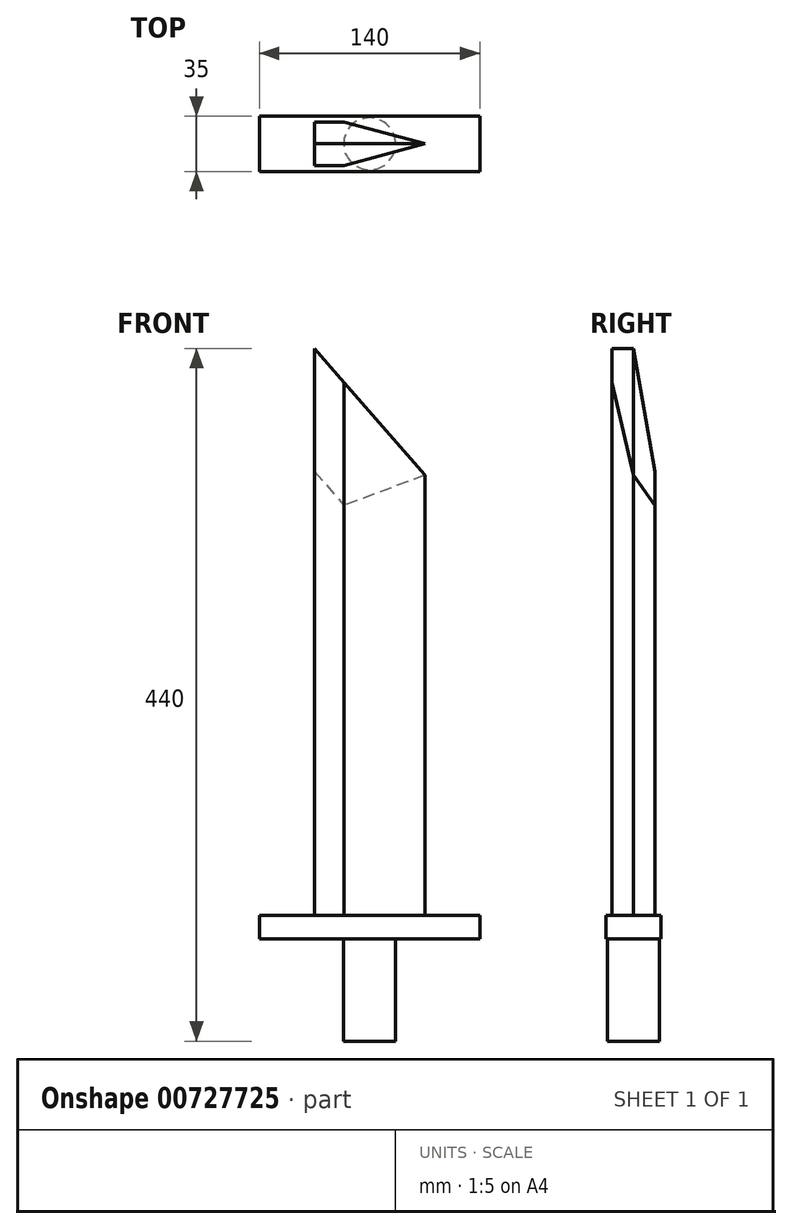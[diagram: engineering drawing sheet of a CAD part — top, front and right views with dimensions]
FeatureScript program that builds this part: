
annotation { "Feature Type Name" : "Feature", "Feature Type Description" : "" }
export const myFeature = defineFeature(function(context is Context, id is Id, definition is map)
    precondition{}
    {
        {
            var Q0;
            Q0=qCreatedBy(makeId("Top.planeOp"),FACE);
            var sketch = newSketch(context, id + "F0", { "sketchPlane" : qUnion([Q0])});
            skCircle(sketch, "E0", {"center": v(0, 0) * mm, "radius": 16.5 * mm});
            skSolve(sketch);
        }
        {
            var Q0;
            Q0=makeQuery(id+"F0.imprint","IMPRINT",FACE,{"disambiguationData":[TD([[makeQuery(id+"F0.imprint","IMPRINT",EDGE,{"derivedFrom":sQuery(id+"F0.wireOp",EDGE,"E0")}),1.0]])]});
            extrude(context, id + "F1", {"entities" : qUnion([Q0]), "oppositeDirection" : true, "depth" : 80 * mm, "offsetDistance" : 25 * mm});
        }
        {
            var Q0;
            Q0=makeQuery(id+"F1.opExtrude","CAP_FACE",FACE,{"disambiguationData":[OSD([sQuery(id+"F0.wireOp",EDGE,"E0")])],"isStart":true});
            var sketch = newSketch(context, id + "F2", { "sketchPlane" : qUnion([Q0])});
            skLineSegment(sketch, "E1.bottom", {"start": v(-70, 17.5) * mm, "end": v(70, 17.5) * mm});
            skLineSegment(sketch, "E1.top", {"start": v(-70, -17.5) * mm, "end": v(70, -17.5) * mm});
            skLineSegment(sketch, "E1.left", {"start": v(-70, 17.5) * mm, "end": v(-70, -17.5) * mm});
            skLineSegment(sketch, "E1.right", {"start": v(70, 17.5) * mm, "end": v(70, -17.5) * mm});
            skPoint(sketch, "E1.middle", {"position": v(0, 0) * mm});
            skSolve(sketch);
        }
        {
            var Q0;
            Q0=makeQuery(id+"F2.imprint","IMPRINT",FACE,{"disambiguationData":[TD([[makeQuery(id+"F2.imprint","IMPRINT",EDGE,{"derivedFrom":sQuery(id+"F2.wireOp",EDGE,"E1.bottom")}),-1.0]])]});
            extrude(context, id + "F3", {"entities" : qUnion([Q0]), "operationType" : NewBodyOperationType.ADD, "oppositeDirection" : true, "depth" : 15 * mm, "offsetDistance" : 25 * mm});
        }
        {
            var Q0;
            {var subQ0=sQuery(id+"F0.wireOp",EDGE,"E0");Q0=makeQuery(id+"F3.boolean.opBoolean","MERGE",FACE,{"derivedFrom":[makeQuery(id+"F1.opExtrude","CAP_FACE",FACE,{"disambiguationData":[OSD([subQ0])],"isStart":true}),makeQuery(id+"F3.opExtrude","CAP_FACE",FACE,{"disambiguationData":[OSD([subQ0,sQuery(id+"F2.wireOp",EDGE,"E1.bottom"),sQuery(id+"F2.wireOp",EDGE,"E1.top"),sQuery(id+"F2.wireOp",EDGE,"E1.left"),sQuery(id+"F2.wireOp",EDGE,"E1.right")])],"isStart":true})]});}
            var sketch = newSketch(context, id + "F4", { "sketchPlane" : qUnion([Q0])});
            skLineSegment(sketch, "E2.bottom", {"start": v(-35, 13.75) * mm, "end": v(35, 13.75) * mm});
            skLineSegment(sketch, "E2.top", {"start": v(-35, -13.75) * mm, "end": v(35, -13.75) * mm});
            skLineSegment(sketch, "E2.left", {"start": v(-35, 13.75) * mm, "end": v(-35, -13.75) * mm});
            skLineSegment(sketch, "E2.right", {"start": v(35, 13.75) * mm, "end": v(35, -13.75) * mm});
            skPoint(sketch, "E2.middle", {"position": v(0, 0) * mm});
            skSolve(sketch);
        }
        {
            var Q0;
            Q0=makeQuery(id+"F4.imprint","IMPRINT",FACE,{"disambiguationData":[TD([[makeQuery(id+"F4.imprint","IMPRINT",EDGE,{"derivedFrom":sQuery(id+"F4.wireOp",EDGE,"E2.bottom")}),-1.0]])]});
            extrude(context, id + "F5", {"entities" : qUnion([Q0]), "operationType" : NewBodyOperationType.ADD, "depth" : 360 * mm, "offsetDistance" : 25 * mm});
        }
        {
            var Q0;
            Q0=makeQuery(id+"F5.opExtrude","SWEPT_FACE",FACE,{"disambiguationData":[OSD([sQuery(id+"F4.wireOp",EDGE,"E2.top")])]});
            var sketch = newSketch(context, id + "F6", { "sketchPlane" : qUnion([Q0])});
            skLineSegment(sketch, "E3", {"start": v(-35, 360) * mm, "end": v(35, 279.53) * mm});
            skSolve(sketch);
        }
        {
            var Q0;
            {var subQ0=sQuery(id+"F6.wireOp",EDGE,"E3");Q0=makeQuery(id+"F6.imprint","IMPRINT",FACE,{"disambiguationData":[TD([[makeQuery(id+"F6.imprint","IMPRINT",EDGE,{"derivedFrom":subQ0}),1.0]])]});}
            extrude(context, id + "F7", {"entities" : qUnion([Q0]), "operationType" : NewBodyOperationType.REMOVE, "oppositeDirection" : true, "depth" : 50 * mm, "offsetDistance" : 25 * mm});
        }
        {
            var Q0;
            Q0=makeQuery(id+"F5.opExtrude","SWEPT_EDGE",EDGE,{"disambiguationData":[OSD([sQuery(id+"F4.wireOp",EDGE,"E2.top"),sQuery(id+"F4.wireOp",EDGE,"E2.right")])]});
            var Q1;
            Q1=makeQuery(id+"F5.opExtrude","SWEPT_EDGE",EDGE,{"disambiguationData":[OSD([sQuery(id+"F4.wireOp",EDGE,"E2.bottom"),sQuery(id+"F4.wireOp",EDGE,"E2.right")])]});
            var Q2;
            Q2=makeQuery(id+"F7.boolean.opBoolean","COPY",EDGE,{"derivedFrom":makeQuery(id+"F7.opExtrude","CAP_EDGE",EDGE,{"disambiguationData":[OSD([sQuery(id+"F6.wireOp",EDGE,"E3")])],"isStart":true})});
            var Q3;
            Q3=makeQuery(id+"F7.boolean.opBoolean","INTERSECT",EDGE,{"derivedFrom":[makeQuery(id+"F5.opExtrude","SWEPT_FACE",FACE,{"disambiguationData":[OSD([sQuery(id+"F4.wireOp",EDGE,"E2.bottom")])]}),makeQuery(id+"F7.opExtrude","SWEPT_FACE",FACE,{"disambiguationData":[OSD([sQuery(id+"F6.wireOp",EDGE,"E3")])]})]});
            chamfer(context, id + "F8", {"entities" : qUnion([Q0, Q1, Q2, Q3]), "chamferType" : ChamferType.OFFSET_ANGLE, "width" : 13.75 * mm, "oppositeDirection" : false, "angle" : 75 * degree, "tangentPropagation" : true});
        }
    });
